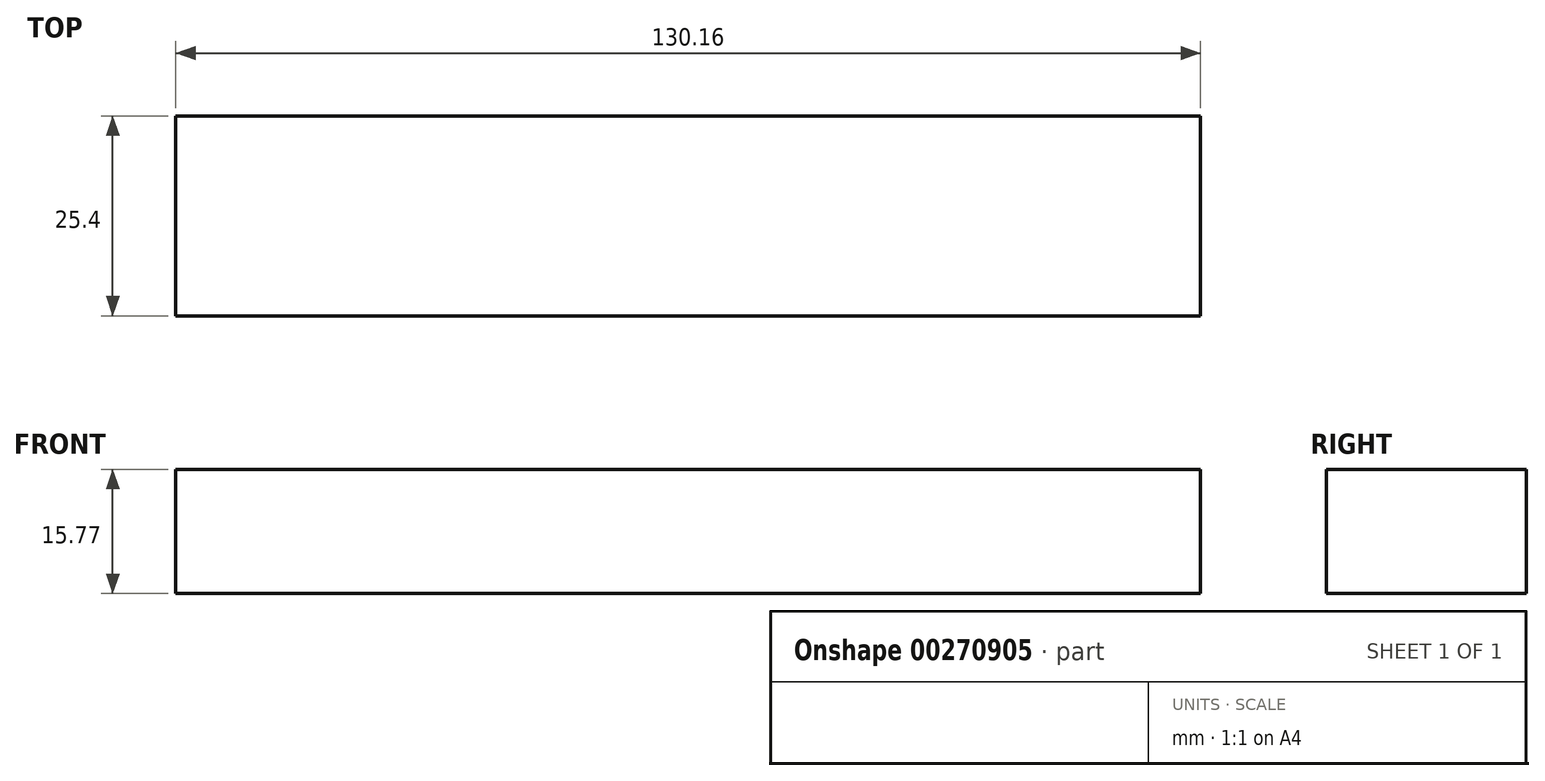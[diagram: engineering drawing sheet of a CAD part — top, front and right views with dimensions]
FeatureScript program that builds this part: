
annotation { "Feature Type Name" : "Feature", "Feature Type Description" : "" }
export const myFeature = defineFeature(function(context is Context, id is Id, definition is map)
    precondition{}
    {
        {
            var Q0;
            Q0=qCreatedBy(makeId("Front.planeOp"),FACE);
            var sketch = newSketch(context, id + "F0", { "sketchPlane" : qUnion([Q0])});
            skLineSegment(sketch, "E0.bottom", {"start": v(-68.74, -62.54) * mm, "end": v(61.42, -62.54) * mm});
            skLineSegment(sketch, "E0.top", {"start": v(-68.74, -46.77) * mm, "end": v(61.42, -46.77) * mm});
            skLineSegment(sketch, "E0.left", {"start": v(-68.74, -62.54) * mm, "end": v(-68.74, -46.77) * mm});
            skLineSegment(sketch, "E0.right", {"start": v(61.42, -62.54) * mm, "end": v(61.42, -46.77) * mm});
            skSolve(sketch);
        }
        {
            var Q0;
            Q0 = qSketchRegion(id + "F0", true);
            extrude(context, id + "F1", {"entities" : qUnion([Q0]), "depth" : 25.4 * mm});
        }
    });
